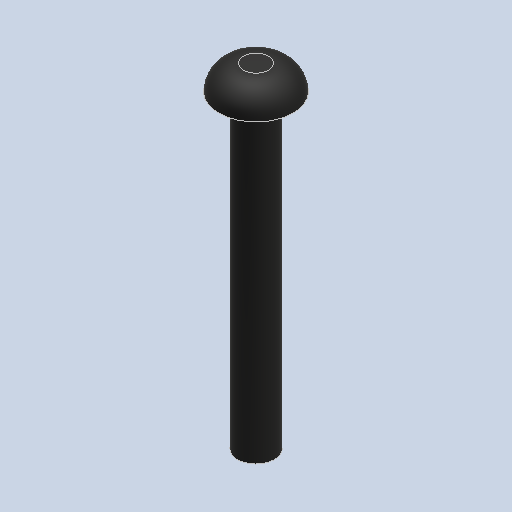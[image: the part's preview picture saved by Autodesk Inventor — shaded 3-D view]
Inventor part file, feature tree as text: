
AUTODESK INVENTOR PART (.ipt)
format: ipt  version: 2023 (Build 270158030, 158C)  size: 245,248 bytes
history: native  units: mm
features: extrude x2, sketch x2, other x1, fillet x1
ambient origin geometry x8: Origin, YZ Plane, XZ Plane, XY Plane, X Axis, Y Axis, Z Axis, Center Point
bodies: Body1 (feature_tree)
feature tree (6):
  other  "ソリッド1"
  extrude  "押し出し1"  Depth=3.0mm
  extrude  "押し出し2"  Depth=25.0mm TaperAngle=0.0deg
  fillet  "フィレット1"  Radius=6.0mm
  sketch  "スケッチ1"
  sketch  "スケッチ2"
